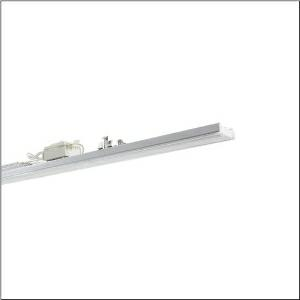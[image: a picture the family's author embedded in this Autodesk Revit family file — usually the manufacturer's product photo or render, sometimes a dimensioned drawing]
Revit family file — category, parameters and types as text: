
# Revit family: licross_r__11_recessed_ho_51te1wdv465m_bae4
name_source: partatom
category: Lighting Fixtures
units: mm (PartAtom-declared; Revit-internal decimal feet)

## family parameters
Cut with Voids When Loaded = No
Host = Face
Light Source = No
Part Type = Normal
Room Calculation Point = No
Round Connector Dimension = Use Diameter
Shared = No

## types (1)
- --- (1 x LED, 6760 lm, 34.7 W, 4000K)
    Apparent Load = 35 VA
    CIE Flux Codes = 73 94 99 100 100
    Color Rendering = 80
    Color Temperature = 4000K
    Default Elevation = 1800 mm
    Description = Licross® 11 Recessed HO, luminaire insert, of sheet steel, coil coated, white, length: 2.250mm, width: 66mm, height: 67mm, LED rated luminous flux: 6.760lm, light colour: 840, control gear: DALI 2, with plug, 5-pole, with phase selection, mains connection: 220..240V, AC, 50/60Hz, rated input power: 35W, halogen-free wiring, primary optical cover: cover, of PMMA, light emission: direct distribution, primary light characteristic: symmetric, protection rating (complete): IP54, insulation class (complete): insulation class I (protective earthing), certification: CE, ENEC, VDE, UKCA, protection symbol: D if used in an environment without relevant dust loads with corresponding accessories, impact resistance: IK06, permissible ambient temperature for indoor applications: -25..+40°C, corresponds to IFS (International Featured Standards) requirements for safety and quality in the food industry, reducing of maximum allowable ambient temperature of 5°C with ceiling mounting, LABS conformity tested according to VDMA 24364:2018-05, packaging unit: 1 piece
    Height = 58 mm
    Lamp = 1 x LED
    Lamp Light Flux = 6760 lm
    Lamp Power = 34.7 W
    Lamp count = 1
    Length = 2250 mm
    Luminous efficacy = 195 lm/W
    Manufacturer = Siteco
    ModVariant = No
    Model = 51TE1WDV465M
    Mounting Place = Ceiling
    Mounting Type = Pendant
    Number of Poles = 1
    OnlyDefault = Yes
    Power Factor = 1
    Product Name = Licross® 11 Recessed HO
    Product group = luminaire insert
    ProductGroupID = 902
    Protection Class = Protection class I
    Protection Degree = IP 54
    RLX_Detail_Level = 1
    RLX_Emergency_Light_Flux = 0 lm
    RLX_Emergency_Type = 0
    RLX_Emergency_Type_DB = No
    RlxData = <blob elided: 29153 chars, md5=f2134124>
    Socket = socket
    Standby Power = 0 W
    System Light Flux = 6760 lm
    System Power = 35 W
    Type Comments = factory setting: luminous flux: 100 % | dim-lin: 254 | 158 mA
    Type Image = l_1296930.jpg
    URL = http://relux.com
    VarID = @adj_022826
    Voltage = 0 V
    Weight = 0.00 kg
    Width = 66 mm

## geometry (parser evidence)
native form markers: Blend x4, Sweep x9
no freeform markers — native parametric forms only
